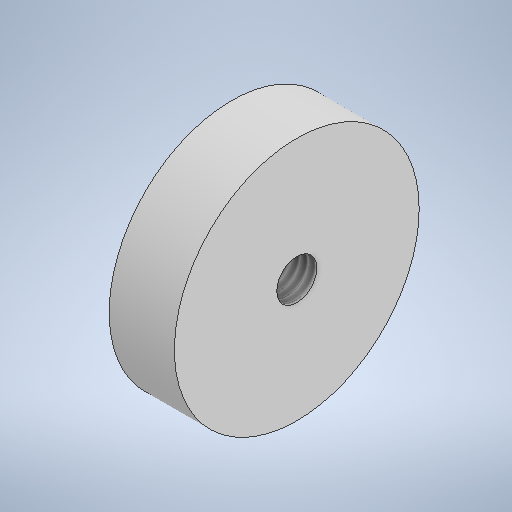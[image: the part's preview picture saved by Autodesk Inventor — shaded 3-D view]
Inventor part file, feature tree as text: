
AUTODESK INVENTOR PART (.ipt)
format: ipt  version: 2025.1 (Build 291241000, 241)  size: 272,384 bytes
history: native  units: mm
features: sketch x2, revolve x1, hole x1
ambient origin geometry x8: Origin, YZ Plane, XZ Plane, XY Plane, X Axis, Y Axis, Z Axis, Center Point
bodies: Solid1 (feature_tree)
feature tree (4):
  revolve  "Revolution1"  [1 undecoded]
  hole  "Hole1"  [1 undecoded]
  sketch  "Sketch1"  dims[d0=15.0mm d1=7.0mm]
  sketch  "Sketch2"  dims[d2=4.0mm d3=5.0mm d4=90.0deg d5=2.459mm d6=6.0mm d7=4.0mm d8=2.0mm d9=90.0deg d10=8.8mm d11=0.0mm]
note: 2 required parameter values undecoded (feature->parameter linkage not recoverable at this tier; creation-order binding heuristic only, values carry confidence <= 0.55)